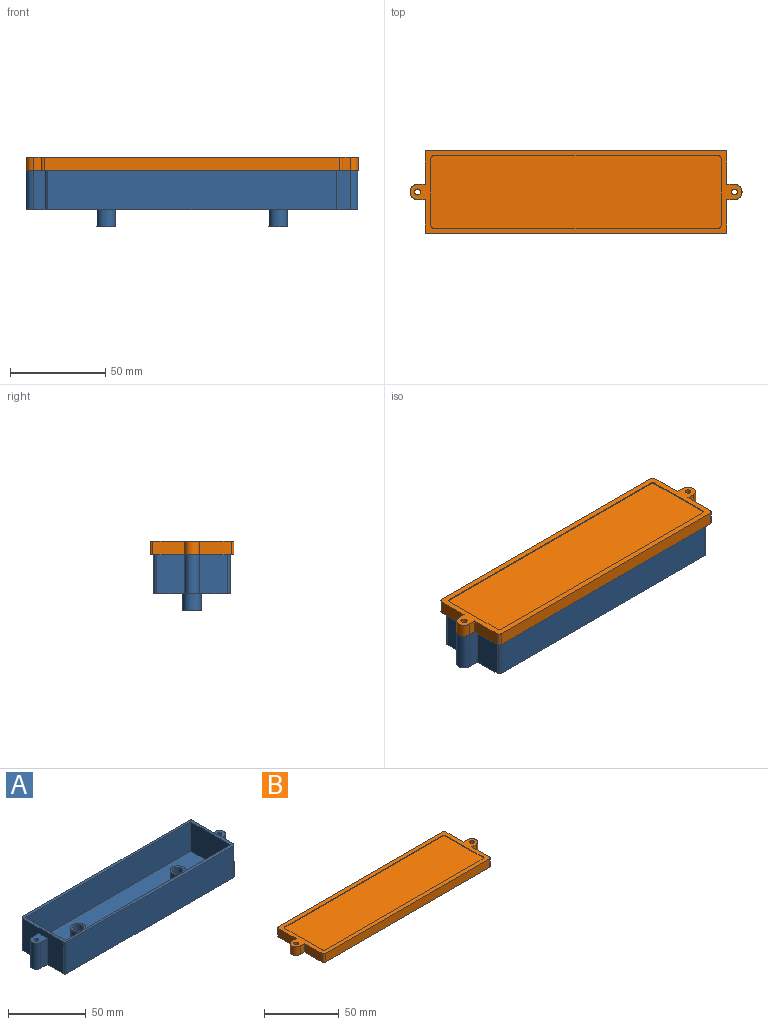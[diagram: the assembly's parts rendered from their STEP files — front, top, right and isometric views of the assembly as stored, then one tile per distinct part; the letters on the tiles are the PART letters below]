
ASSEMBLY  parts=2 mates=1
PART A: 35 faces, bbox 174.4x40.1x34 mm
  f0: plane 37.1x25mm, normal (-1,0,0), area 763.5mm2, adj f2,f5,f11,f14,f30,f31,f34
  f1: plane 37.1x25mm, normal (1,0,0), area 763.5mm2, adj f2,f5,f12,f13,f25,f26,f29
  f2: plane 154.4x40.1mm, normal (0,0,1), area 760.1mm2, adj f0,f1,f3,f4,f6,f7,f8,f9
  f3: plane 151.4x25mm, normal (0,-1,0), area 3785mm2, adj f2,f5,f11,f12
  f4: plane 151.4x25mm, normal (0,1,0), area 3785mm2, adj f2,f5,f13,f14
  f5: plane 174.4x40.1mm, normal (0,0,-1), area 6169.1mm2, adj f0,f1,f3,f4,f11,f12,f13,f14
  f6: plane 36.1x23mm, normal (1,0,0), area 830.3mm2, adj f2,f7,f9,f10
  f7: plane 150.4x23mm, normal (0,1,0), area 3459.2mm2, adj f2,f6,f8,f10
  f8: plane 36.1x23mm, normal (-1,0,0), area 830.3mm2, adj f2,f7,f9,f10
  f9: plane 150.4x23mm, normal (0,-1,0), area 3459.2mm2, adj f2,f6,f8,f10
  f10: plane 150.4x36.1mm, normal (0,0,1), area 5278.6mm2, adj f6,f7,f8,f9,f16,f21
  f11: cylinder r=1.5mm len=25mm, axis (0,0,1), area 58.9mm2, adj f0,f2,f3,f5
  f12: cylinder r=1.5mm len=25mm, axis (0,0,-1), area 58.9mm2, adj f1,f2,f3,f5
  f13: cylinder r=1.5mm len=25mm, axis (0,0,1), area 58.9mm2, adj f1,f2,f4,f5
  f14: cylinder r=1.5mm len=25mm, axis (0,0,-1), area 58.9mm2, adj f0,f2,f4,f5
  f15: plane 9.8x9.8mm, normal (0,0,1), area 39.1mm2, adj f16,f17
  f16: cylinder r=4.9mm len=9.8mm, axis (0,0,1), area 277.1mm2, adj f10,f15
  f17: cylinder r=3.4mm len=20mm, axis (0,0,1), area 427.3mm2, adj f15,f19
  f18: cylinder r=4.9mm len=9.8mm, axis (0,0,1), area 277.1mm2, adj f5,f19
  f19: plane 9.8x9.8mm, normal (0,0,-1), area 39.1mm2, adj f17,f18
  f20: plane 9.8x9.8mm, normal (0,0,1), area 39.1mm2, adj f21,f22
  f21: cylinder r=4.9mm len=9.8mm, axis (0,0,1), area 277.1mm2, adj f10,f20
  f22: cylinder r=3.4mm len=20mm, axis (0,0,1), area 427.3mm2, adj f20,f24
  f23: cylinder r=4.9mm len=9.8mm, axis (0,0,1), area 277.1mm2, adj f5,f24
  f24: plane 9.8x9.8mm, normal (0,0,-1), area 39.1mm2, adj f22,f23
  f25: plane 20.5x6mm, normal (0,1,0), area 123mm2, adj f1,f5,f27,f29
  f26: plane 20.5x6mm, normal (0,-1,0), area 123mm2, adj f1,f5,f27,f29
  f27: cylinder r=4mm len=20.5mm, axis (0,0,-1), area 257.6mm2, adj f5,f25,f26,f29
  f28: cylinder r=1.59mm len=20.5mm, axis (0,0,-1), area 204.5mm2, adj f5,f29
  f29: plane 10x8mm, normal (0,0,1), area 65.2mm2, adj f1,f25,f26,f27,f28
  f30: plane 20.5x6mm, normal (0,-1,0), area 123mm2, adj f0,f5,f32,f34
  f31: plane 20.5x6mm, normal (0,1,0), area 123mm2, adj f0,f5,f32,f34
  f32: cylinder r=4mm len=20.5mm, axis (0,0,-1), area 257.6mm2, adj f5,f30,f31,f34
  f33: cylinder r=1.59mm len=20.5mm, axis (0,0,-1), area 204.5mm2, adj f5,f34
  f34: plane 10x8mm, normal (0,0,1), area 65.2mm2, adj f0,f30,f31,f32,f33
PART B: 38 faces, bbox 174.4x44.1x7 mm
  f0: plane 16.55x7mm, normal (1,0,0), area 115.8mm2, adj f2,f3,f27,f34
  f1: plane 16.55x7mm, normal (-1,0,0), area 115.8mm2, adj f2,f3,f29,f32
  f2: plane 174.4x44.1mm, normal (0,0,-1), area 893.3mm2, adj f0,f1,f4,f5,f6,f7,f14,f15
  f3: plane 174.4x44.1mm, normal (0,0,1), area 1278.3mm2, adj f0,f1,f4,f5,f6,f7,f8,f9
  f4: plane 16.55x7mm, normal (-1,0,0), area 115.8mm2, adj f2,f3,f26,f30
  f5: plane 155.4x7mm, normal (0,-1,0), area 1087.8mm2, adj f2,f3,f26,f27
  f6: plane 16.55x7mm, normal (1,0,0), area 115.8mm2, adj f2,f3,f28,f37
  f7: plane 155.4x7mm, normal (0,1,0), area 1087.8mm2, adj f2,f3,f28,f29
  f8: plane 35.1x0.5mm, normal (1,0,0), area 17.6mm2, adj f3,f12,f22,f25
  f9: plane 149.4x0.5mm, normal (0,1,0), area 74.7mm2, adj f3,f12,f22,f23
  f10: plane 35.1x0.5mm, normal (-1,0,0), area 17.6mm2, adj f3,f12,f23,f24
  f11: plane 149.4x0.5mm, normal (0,-1,0), area 74.7mm2, adj f3,f12,f24,f25
  f12: plane 152.4x38.1mm, normal (0,0,1), area 5804.5mm2, adj f8,f9,f10,f11,f22,f23,f24,f25
  f13: plane 154.4x40.1mm, normal (0,0,-1), area 6189.5mm2, adj f14,f15,f16,f17,f18,f19,f20,f21
  f14: plane 37.1x4.5mm, normal (1,0,0), area 166.9mm2, adj f2,f13,f20,f21
  f15: plane 151.4x4.5mm, normal (0,1,0), area 681.3mm2, adj f2,f13,f18,f21
  f16: plane 37.1x4.5mm, normal (-1,0,0), area 166.9mm2, adj f2,f13,f18,f19
  f17: plane 151.4x4.5mm, normal (0,-1,0), area 681.3mm2, adj f2,f13,f19,f20
  f18: cylinder r=1.5mm len=4.5mm, axis (0,0,-1), area 10.6mm2, adj f2,f13,f15,f16
  f19: cylinder r=1.5mm len=4.5mm, axis (0,0,1), area 10.6mm2, adj f2,f13,f16,f17
  f20: cylinder r=1.5mm len=4.5mm, axis (0,0,-1), area 10.6mm2, adj f2,f13,f14,f17
  f21: cylinder r=1.5mm len=4.5mm, axis (0,0,1), area 10.6mm2, adj f2,f13,f14,f15
  f22: cylinder r=1.5mm len=1.5mm, axis (0,0,1), area 1.2mm2, adj f3,f8,f9,f12
  f23: cylinder r=1.5mm len=1.5mm, axis (0,0,-1), area 1.2mm2, adj f3,f9,f10,f12
  f24: cylinder r=1.5mm len=1.5mm, axis (0,0,1), area 1.2mm2, adj f3,f10,f11,f12
  f25: cylinder r=1.5mm len=1.5mm, axis (0,0,-1), area 1.2mm2, adj f3,f8,f11,f12
  f26: cylinder r=1.5mm len=7mm, axis (0,0,-1), area 16.5mm2, adj f2,f3,f4,f5
  f27: cylinder r=1.5mm len=7mm, axis (0,0,1), area 16.5mm2, adj f0,f2,f3,f5
  f28: cylinder r=1.5mm len=7mm, axis (0,0,-1), area 16.5mm2, adj f2,f3,f6,f7
  f29: cylinder r=1.5mm len=7mm, axis (0,0,1), area 16.5mm2, adj f1,f2,f3,f7
  f30: plane 7x4mm, normal (0,-1,0), area 28mm2, adj f2,f3,f4,f31
  f31: cylinder r=4mm len=8mm, axis (0,0,1), area 88mm2, adj f2,f3,f30,f32
  f32: plane 7x4mm, normal (0,1,0), area 28mm2, adj f1,f2,f3,f31
  f33: cylinder r=1.59mm len=7mm, axis (0,0,1), area 69.8mm2, adj f2,f3
  f34: plane 7x4mm, normal (0,-1,0), area 28mm2, adj f0,f2,f3,f35
  f35: cylinder r=4mm len=8mm, axis (0,0,1), area 88mm2, adj f2,f3,f34,f37
  f36: cylinder r=1.5mm len=7mm, axis (0,0,1), area 66mm2, adj f2,f3
  f37: plane 7x4mm, normal (0,1,0), area 28mm2, adj f2,f3,f6,f35
PLACE A t=(-65.58,26.92,14.02)mm
PLACE B t=(-67.58,24.92,41.52)mm
MATE fastened A.f2 <-> B.f13  axis (0,0,1) through (11.62,46.97,39.02)mm
